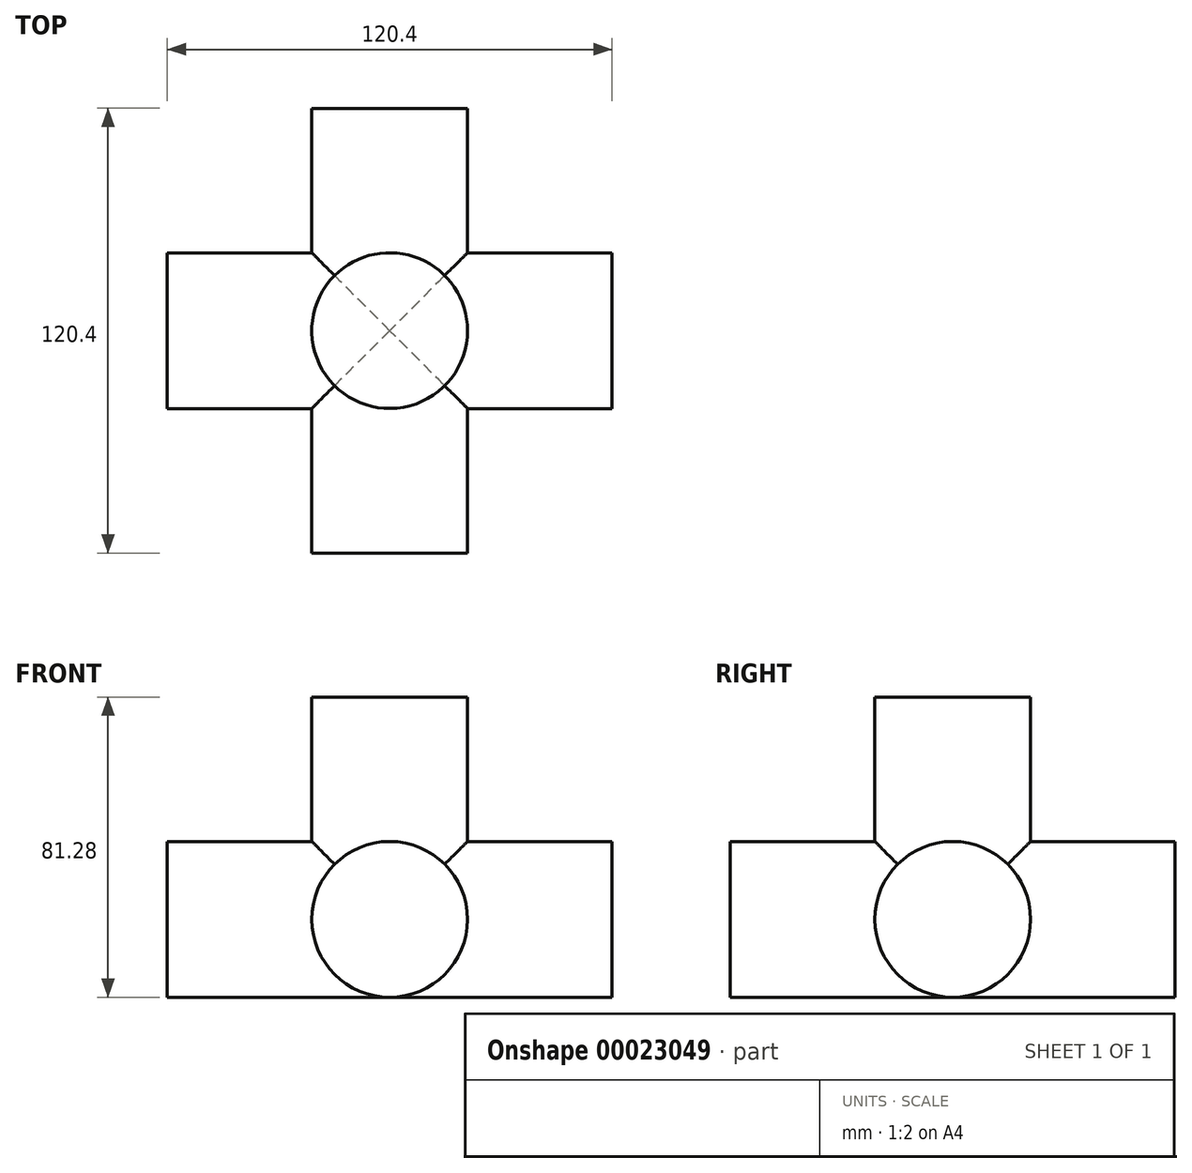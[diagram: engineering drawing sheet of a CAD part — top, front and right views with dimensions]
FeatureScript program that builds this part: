
annotation { "Feature Type Name" : "Feature", "Feature Type Description" : "" }
export const myFeature = defineFeature(function(context is Context, id is Id, definition is map)
    precondition{}
    {
        {
            var Q0;
            Q0=qCreatedBy(makeId("Front.planeOp"),FACE);
            var sketch = newSketch(context, id + "F0", { "sketchPlane" : qUnion([Q0])});
            skCircle(sketch, "E0", {"center": v(0, 0) * mm, "radius": 21.08 * mm});
            skSolve(sketch);
        }
        {
            var Q0;
            Q0=qCreatedBy(makeId("Top.planeOp"),FACE);
            var sketch = newSketch(context, id + "F1", { "sketchPlane" : qUnion([Q0])});
            skCircle(sketch, "E1", {"center": v(0, 0) * mm, "radius": 21.08 * mm});
            skSolve(sketch);
        }
        {
            var Q0;
            Q0=makeQuery(id+"F1.imprint","IMPRINT",FACE,{"disambiguationData":[TD([[makeQuery(id+"F1.imprint","IMPRINT",EDGE,{"derivedFrom":sQuery(id+"F1.wireOp",EDGE,"E1")}),1.0]])]});
            extrude(context, id + "F2", {"entities" : qUnion([Q0]), "depth" : 60.2 * mm});
        }
        {
            var Q0;
            Q0=makeQuery(id+"F0.imprint","IMPRINT",FACE,{"disambiguationData":[TD([[makeQuery(id+"F0.imprint","IMPRINT",EDGE,{"derivedFrom":sQuery(id+"F0.wireOp",EDGE,"E0")}),1.0]])]});
            extrude(context, id + "F3", {"entities" : qUnion([Q0]), "operationType" : NewBodyOperationType.ADD, "depth" : 60.2 * mm});
        }
        {
            var Q0;
            Q0 = qSketchRegion(id + "F0", true);
            extrude(context, id + "F4", {"entities" : qUnion([Q0]), "operationType" : NewBodyOperationType.ADD, "oppositeDirection" : true, "depth" : 60.2 * mm});
        }
        {
            var Q0;
            Q0=qCreatedBy(makeId("Right.planeOp"),FACE);
            var sketch = newSketch(context, id + "F5", { "sketchPlane" : qUnion([Q0])});
            skCircle(sketch, "E2", {"center": v(0, 0) * mm, "radius": 21.08 * mm});
            skSolve(sketch);
        }
        {
            var Q0;
            Q0 = qSketchRegion(id + "F5", true);
            extrude(context, id + "F6", {"entities" : qUnion([Q0]), "operationType" : NewBodyOperationType.ADD, "depth" : 60.2 * mm});
        }
        {
            var Q0;
            Q0 = qSketchRegion(id + "F5", true);
            extrude(context, id + "F7", {"entities" : qUnion([Q0]), "operationType" : NewBodyOperationType.ADD, "oppositeDirection" : true, "depth" : 60.2 * mm});
        }
    });
